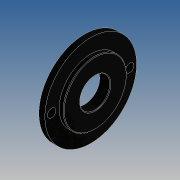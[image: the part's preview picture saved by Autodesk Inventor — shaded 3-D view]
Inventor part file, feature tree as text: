
AUTODESK INVENTOR PART (.ipt)
format: ipt  version: 2015 SP1 (Build 190203100, 203)  size: 225,280 bytes
history: native  units: mm
features: sketch x2, revolve x1, hole x1, mirror x1, fillet x1
ambient origin geometry x8: Origin, YZ Plane, XZ Plane, XY Plane, X Axis, Y Axis, Z Axis, Center Point
bodies: Solid1 (feature_tree)
feature tree (6):
  revolve  "Revolution1"  [1 undecoded]
  hole  "Hole1"  [1 undecoded]
  mirror  "Mirror1"
  fillet  "Fillet1"  Radius=30.5mm
  sketch  "Sketch1"  dims[d0=10.0mm d1=21.0mm]
  sketch  "Sketch2"  dims[d2=1.5mm d3=2.0mm d4=30.5mm d5=90.0deg d6=13.0mm d7=2.8mm d8=6.0mm d9=4.0mm d10=2.0mm d11=90.0deg d12=8.0mm d13=20.594885mm d14=0.2mm]
note: 2 required parameter values undecoded (feature->parameter linkage not recoverable at this tier; creation-order binding heuristic only, values carry confidence <= 0.55)